# Revit family: VLGFL1001-xxxWS8xxB0550
name_source: partatom
category: Leuchten
revit_build: Autodesk Revit 2017 (Build: 20160225_1515(x64)
units: mm (PartAtom-declared; Revit-internal decimal feet)

## family parameters
Basisbauteil = Fläche
Beim Laden mit Abzugskörper schneiden = Nein
Bemaßung runder Anschluss = Durchmesser verwenden
Gemeinsam genutzt = Nein
Lichtquelle = Ja
OmniClass-Nummer = 23.80.70.11
OmniClass-Titel = Luminaries for Internal Lighting
Raumberechnungspunkt = Nein
Teiletyp = Normal

## types (6) — shared parameters
Baugruppenkennzeichen = D5020200
Datei für fotometrisches Netz = VLGFL1501-5NDWS840B0800.IES
Emissionsform beim Rendern sichtbar = Nein
Farbfilter = 16777215
Farbtemperaturverschiebung bei Dämpfen der Lampe = <Keine Auswahl>
Hersteller = RIDI Leuchten GmbH
Lampe = LED
Neigungswinkel = 90.00°
Scheinlast = 33 VA
URL = www.ridi.de
Von Breite des Rechtecks ausssenden = 969 mm
Von Länge des Rechtecks aussenden = 64 mm  [stored 0.209974 ft]
brand = RIDI
conformity mark = CE
electrical safety class = 1
height = 66 mm  [stored 0.216535 ft]
ingress protection (IP) code = IP54
length = 1000 mm  [stored 3.28084 ft]
nominal frequency = 50-60Hz
nominal voltage = 230
rated input power = 33
voltage type (AC, DC, UC) = AC
weight = 1.4 kg
width = 67 mm
zero-valued in all types: Vorgabe-Ansicht

## per-type parameters (varying)
| type | Modell |
| VLGFL1001-5NDWS840B0550 | 1551066 |
| VLGFL1001-7DAWS840B0550 | 1561066 |
| VLGFL1001-5NDWS850B0550 | 1551074 |
| VLGFL1001-7DAWS850B0550 | 1561074 |
| VLGFL1001-5NDWS865B0550 | 1551082 |
| VLGFL1001-7DAWS865B0550 | 1551082 |

note: column(s) folded — value = type name in every type: product name

note: [stored X ft] marks values corroborated as IEEE doubles in the binary element streams (Revit-internal decimal feet)
